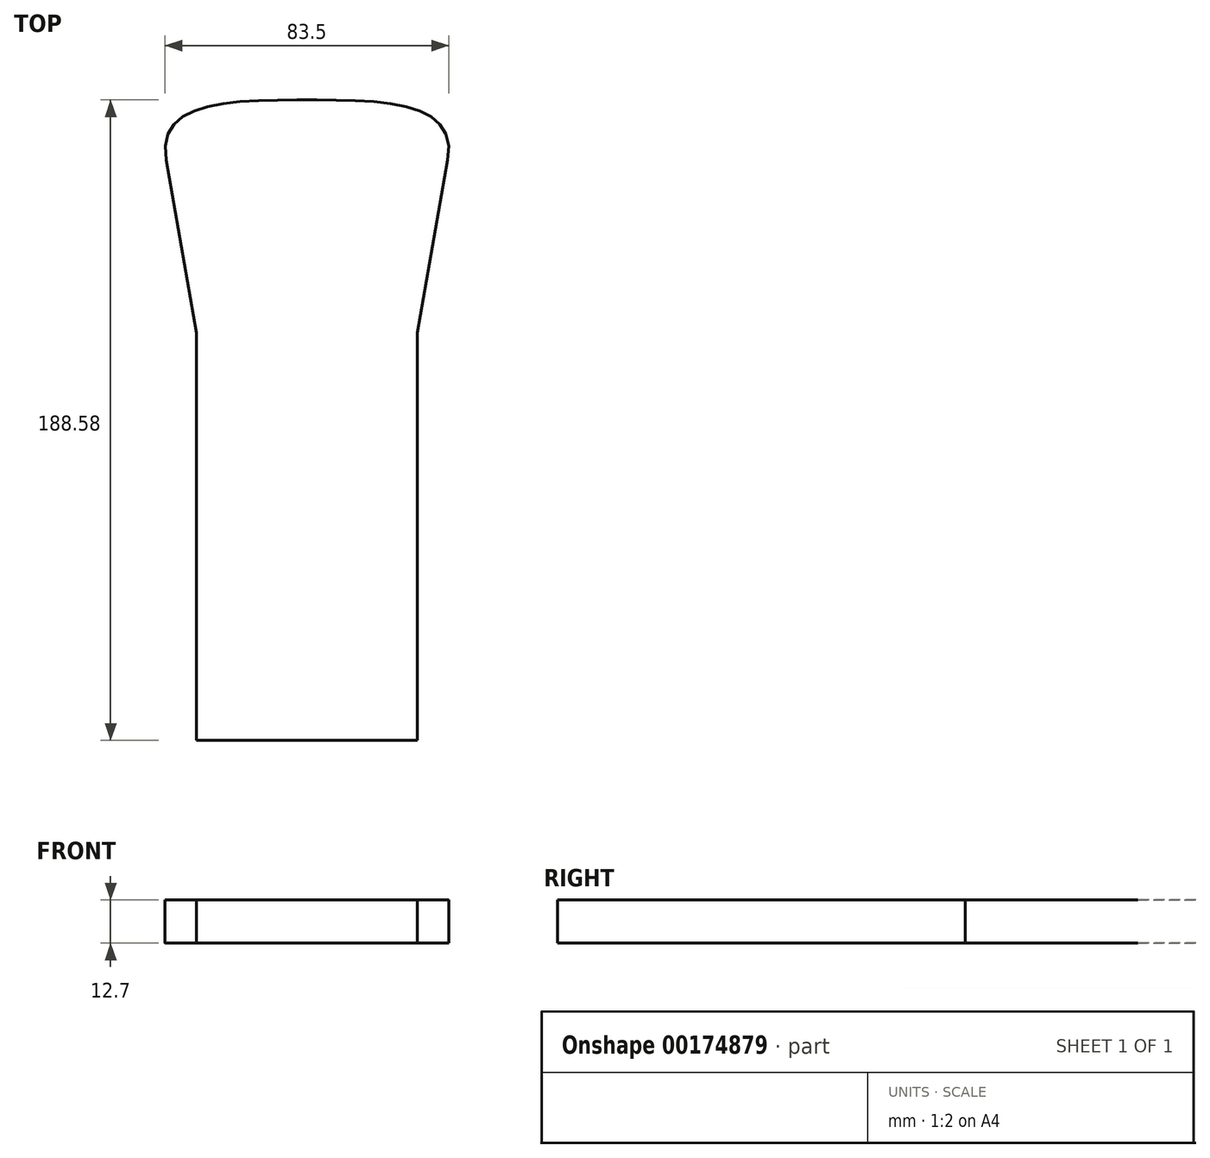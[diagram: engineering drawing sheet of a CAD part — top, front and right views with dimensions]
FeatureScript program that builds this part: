
annotation { "Feature Type Name" : "Feature", "Feature Type Description" : "" }
export const myFeature = defineFeature(function(context is Context, id is Id, definition is map)
    precondition{}
    {
        {
            var Q0;
            Q0=qCreatedBy(makeId("Top.planeOp"),FACE);
            var sketch = newSketch(context, id + "F0", { "sketchPlane" : qUnion([Q0])});
            skLineSegment(sketch, "E0.bottom", {"start": v(-32.5, -60) * mm, "end": v(32.5, -60) * mm});
            skLineSegment(sketch, "E0.top", {"start": v(-32.5, 60) * mm, "end": v(32.5, 60) * mm, "construction": true});
            skLineSegment(sketch, "E0.left", {"start": v(-32.5, -60) * mm, "end": v(-32.5, 60) * mm});
            skLineSegment(sketch, "E0.right", {"start": v(32.5, -60) * mm, "end": v(32.5, 60) * mm});
            skPoint(sketch, "E0.middle", {"position": v(0, 0) * mm});
            skLineSegment(sketch, "E1", {"start": v(-32.5, 60) * mm, "end": v(-41.46, 110.8) * mm});
            skLineSegment(sketch, "E2", {"start": v(0, 0) * mm, "end": v(0, 110.8) * mm, "construction": true});
            skLineSegment(sketch, "E3.MirrorCS", {"start": v(32.5, 60) * mm, "end": v(41.46, 110.8) * mm});
            skFitSpline(sketch, "E4", {"points": [v(-41.46, 110.8) * mm, v(0, 128.58) * mm, v(41.46, 110.8) * mm], "startDerivative": vector(-18.81, 106.68) * mm, "endDerivative": vector(-18.81, -106.68) * mm});
            skSolve(sketch);
        }
        {
            var Q0;
            Q0=makeQuery(id+"F0.imprint","IMPRINT",FACE,{"disambiguationData":[TD([[makeQuery(id+"F0.imprint","IMPRINT",EDGE,{"derivedFrom":sQuery(id+"F0.wireOp",EDGE,"E0.bottom")}),1.0]])]});
            extrude(context, id + "F1", {"entities" : qUnion([Q0]), "depth" : 12.7 * mm});
        }
    });
